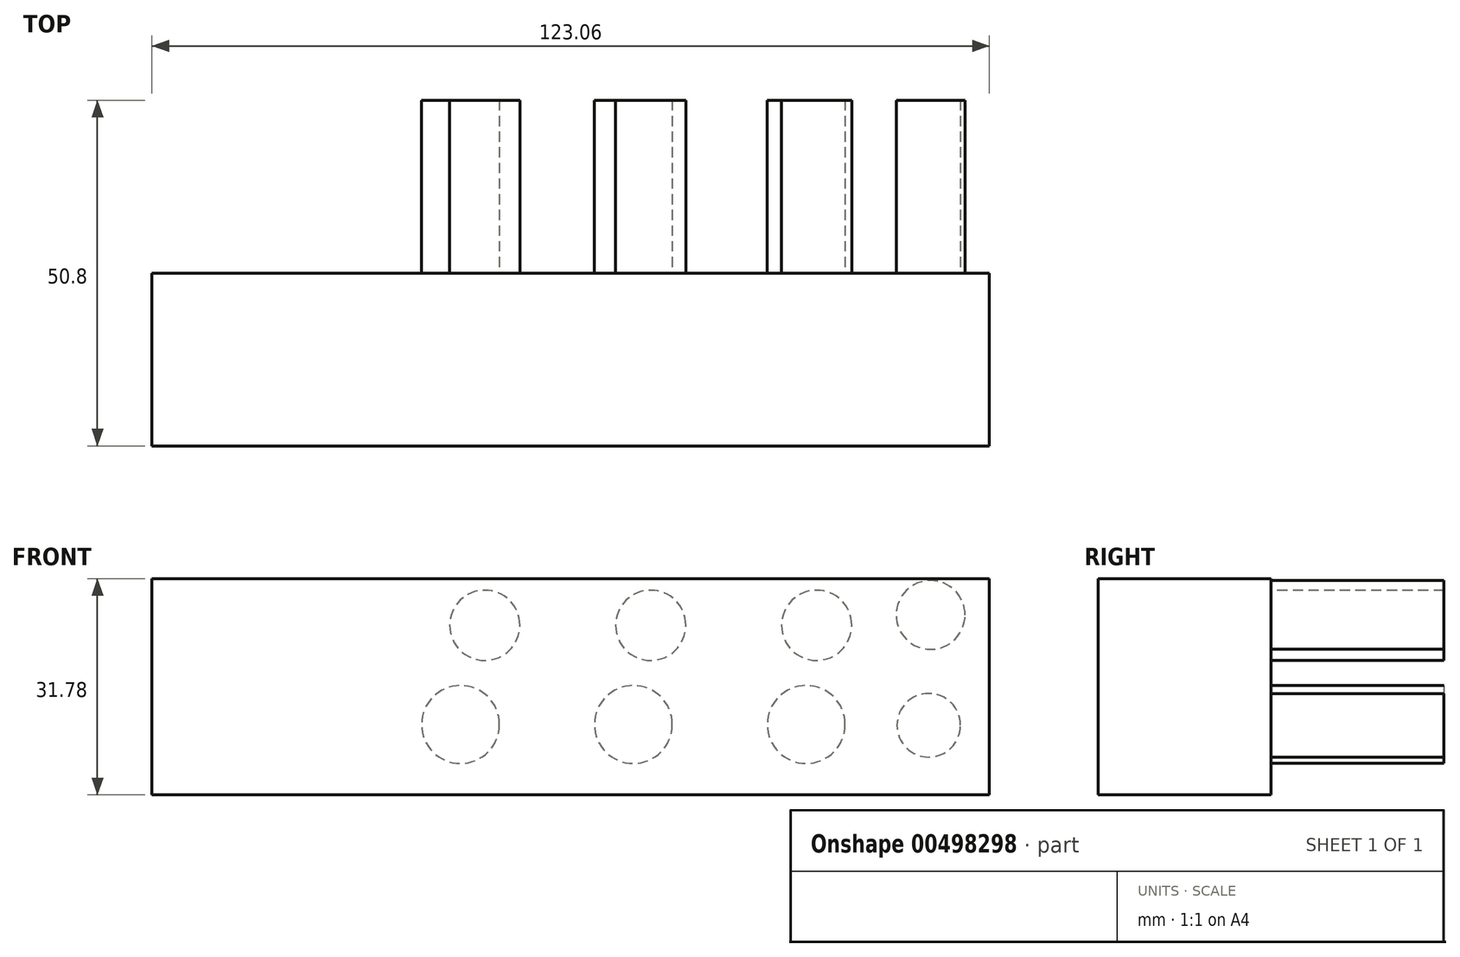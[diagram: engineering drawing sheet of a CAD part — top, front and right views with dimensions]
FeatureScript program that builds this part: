
annotation { "Feature Type Name" : "Feature", "Feature Type Description" : "" }
export const myFeature = defineFeature(function(context is Context, id is Id, definition is map)
    precondition{}
    {
        {
            var Q0;
            Q0=qCreatedBy(makeId("Front.planeOp"),FACE);
            var sketch = newSketch(context, id + "F0", { "sketchPlane" : qUnion([Q0])});
            skLineSegment(sketch, "E0.bottom", {"start": v(-64.24, 37.62) * mm, "end": v(58.82, 37.62) * mm});
            skLineSegment(sketch, "E0.top", {"start": v(-64.24, 69.4) * mm, "end": v(58.82, 69.4) * mm});
            skLineSegment(sketch, "E0.left", {"start": v(-64.24, 37.62) * mm, "end": v(-64.24, 69.4) * mm});
            skLineSegment(sketch, "E0.right", {"start": v(58.82, 37.62) * mm, "end": v(58.82, 69.4) * mm});
            skSolve(sketch);
        }
        {
            var Q0;
            Q0 = qSketchRegion(id + "F0", true);
            extrude(context, id + "F1", {"entities" : qUnion([Q0]), "depth" : 25.4 * mm});
        }
        {
            var Q0;
            Q0=makeQuery(id+"F1.opExtrude","CAP_FACE",FACE,{"disambiguationData":[OSD([sQuery(id+"F0.wireOp",EDGE,"E0.bottom"),sQuery(id+"F0.wireOp",EDGE,"E0.top"),sQuery(id+"F0.wireOp",EDGE,"E0.left"),sQuery(id+"F0.wireOp",EDGE,"E0.right")])],"isStart":true});
            var sketch = newSketch(context, id + "F2", { "sketchPlane" : qUnion([Q0])});
            skCircle(sketch, "E1", {"center": v(-50.2, 64.07) * mm, "radius": 5.06 * mm});
            skSolve(sketch);
        }
        {
            var Q0;
            Q0=makeQuery(id+"F2.imprint","IMPRINT",FACE,{"disambiguationData":[TD([[makeQuery(id+"F2.imprint","IMPRINT",EDGE,{"derivedFrom":sQuery(id+"F2.wireOp",EDGE,"E1")}),1.0]])]});
            var Q1;
            Q1=sQuery(id+"F2.wireOp",EDGE,"E1");
            extrude(context, id + "F3", {"entities" : qUnion([Q0]), "surfaceEntities" : qUnion([Q1]), "depth" : 25.4 * mm});
        }
        {
            var Q0;
            Q0=makeQuery(id+"F1.opExtrude","CAP_FACE",FACE,{"disambiguationData":[OSD([sQuery(id+"F0.wireOp",EDGE,"E0.bottom"),sQuery(id+"F0.wireOp",EDGE,"E0.top"),sQuery(id+"F0.wireOp",EDGE,"E0.left"),sQuery(id+"F0.wireOp",EDGE,"E0.right")])],"isStart":true});
            var sketch = newSketch(context, id + "F4", { "sketchPlane" : qUnion([Q0])});
            skCircle(sketch, "E2", {"center": v(-49.9, 47.86) * mm, "radius": 4.67 * mm});
            skSolve(sketch);
        }
        {
            var Q0;
            Q0=makeQuery(id+"F4.imprint","IMPRINT",FACE,{"disambiguationData":[TD([[makeQuery(id+"F4.imprint","IMPRINT",EDGE,{"derivedFrom":sQuery(id+"F4.wireOp",EDGE,"E2")}),1.0]])]});
            var Q1;
            Q1 = qSketchRegion(id + "F6", true);
            extrude(context, id + "F5", {"entities" : qUnion([Q0, Q1]), "operationType" : NewBodyOperationType.ADD, "depth" : 25.4 * mm});
        }
        {
            var Q0;
            Q0=makeQuery(id+"F1.opExtrude","CAP_FACE",FACE,{"disambiguationData":[OSD([sQuery(id+"F0.wireOp",EDGE,"E0.bottom"),sQuery(id+"F0.wireOp",EDGE,"E0.top"),sQuery(id+"F0.wireOp",EDGE,"E0.left"),sQuery(id+"F0.wireOp",EDGE,"E0.right")])],"isStart":true});
            var sketch = newSketch(context, id + "F6", { "sketchPlane" : qUnion([Q0])});
            skCircle(sketch, "E3", {"center": v(-31.9, 47.97) * mm, "radius": 5.72 * mm});
            skCircle(sketch, "E4.1.0.0", {"center": v(-6.5, 47.97) * mm, "radius": 5.72 * mm});
            skCircle(sketch, "E4.2.0.0", {"center": v(18.9, 47.97) * mm, "radius": 5.72 * mm});
            skLineSegment(sketch, "E4.direction1", {"start": v(-31.9, 47.97) * mm, "end": v(-6.5, 47.97) * mm, "construction": true});
            skSolve(sketch);
        }
        {
            var Q0;
            Q0=makeQuery(id+"F6.imprint","IMPRINT",FACE,{"disambiguationData":[TD([[makeQuery(id+"F6.imprint","IMPRINT",EDGE,{"derivedFrom":sQuery(id+"F6.wireOp",EDGE,"E3")}),1.0]])]});
            var Q1;
            Q1=makeQuery(id+"F6.imprint","IMPRINT",FACE,{"disambiguationData":[TD([[makeQuery(id+"F6.imprint","IMPRINT",EDGE,{"derivedFrom":sQuery(id+"F6.wireOp",EDGE,"E4.1.0.0")}),1.0]])]});
            var Q2;
            Q2=makeQuery(id+"F6.imprint","IMPRINT",FACE,{"disambiguationData":[TD([[makeQuery(id+"F6.imprint","IMPRINT",EDGE,{"derivedFrom":sQuery(id+"F6.wireOp",EDGE,"E4.2.0.0")}),1.0]])]});
            var Q3;
            Q3=sQuery(id+"F6.wireOp",EDGE,"E3");
            var Q4;
            Q4=sQuery(id+"F6.wireOp",EDGE,"E4.1.0.0");
            var Q5;
            Q5=sQuery(id+"F6.wireOp",EDGE,"E4.2.0.0");
            extrude(context, id + "F7", {"entities" : qUnion([Q0, Q1, Q2]), "surfaceEntities" : qUnion([Q3, Q4, Q5]), "depth" : 25.4 * mm});
        }
        {
            var Q0;
            Q0=makeQuery(id+"F1.opExtrude","CAP_FACE",FACE,{"disambiguationData":[OSD([sQuery(id+"F0.wireOp",EDGE,"E0.bottom"),sQuery(id+"F0.wireOp",EDGE,"E0.top"),sQuery(id+"F0.wireOp",EDGE,"E0.left"),sQuery(id+"F0.wireOp",EDGE,"E0.right")])],"isStart":true});
            var sketch = newSketch(context, id + "F8", { "sketchPlane" : qUnion([Q0])});
            skCircle(sketch, "E5", {"center": v(-33.44, 62.54) * mm, "radius": 5.16 * mm});
            skCircle(sketch, "E6.1.0.0", {"center": v(-9.06, 62.54) * mm, "radius": 5.16 * mm});
            skCircle(sketch, "E6.2.0.0", {"center": v(15.33, 62.54) * mm, "radius": 5.16 * mm});
            skLineSegment(sketch, "E6.direction1", {"start": v(-33.44, 62.54) * mm, "end": v(-9.06, 62.54) * mm, "construction": true});
            skSolve(sketch);
        }
        {
            var Q0;
            Q0=makeQuery(id+"F8.imprint","IMPRINT",FACE,{"disambiguationData":[TD([[makeQuery(id+"F8.imprint","IMPRINT",EDGE,{"derivedFrom":sQuery(id+"F8.wireOp",EDGE,"E5")}),1.0]])]});
            var Q1;
            Q1=makeQuery(id+"F8.imprint","IMPRINT",FACE,{"disambiguationData":[TD([[makeQuery(id+"F8.imprint","IMPRINT",EDGE,{"derivedFrom":sQuery(id+"F8.wireOp",EDGE,"E6.1.0.0")}),1.0]])]});
            var Q2;
            Q2=makeQuery(id+"F8.imprint","IMPRINT",FACE,{"disambiguationData":[TD([[makeQuery(id+"F8.imprint","IMPRINT",EDGE,{"derivedFrom":sQuery(id+"F8.wireOp",EDGE,"E6.2.0.0")}),1.0]])]});
            var Q3;
            Q3=sQuery(id+"F8.wireOp",EDGE,"E6.1.0.0");
            var Q4;
            Q4=sQuery(id+"F8.wireOp",EDGE,"E5");
            var Q5;
            Q5=sQuery(id+"F8.wireOp",EDGE,"E6.2.0.0");
            extrude(context, id + "F9", {"entities" : qUnion([Q0, Q1, Q2]), "surfaceEntities" : qUnion([Q3, Q4, Q5]), "depth" : 25.4 * mm});
        }
    });
